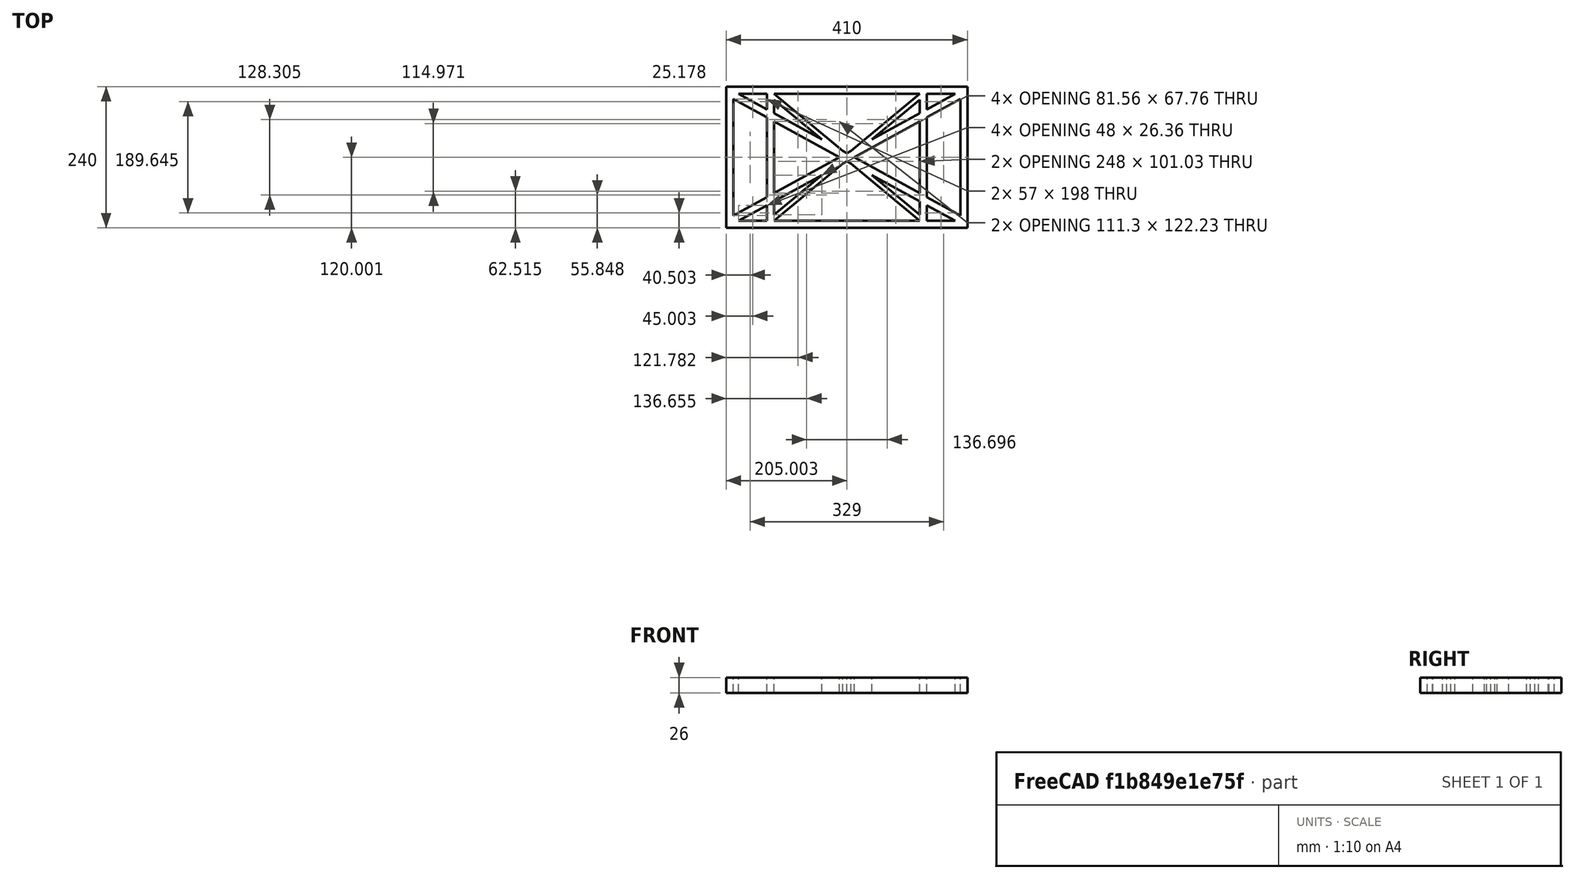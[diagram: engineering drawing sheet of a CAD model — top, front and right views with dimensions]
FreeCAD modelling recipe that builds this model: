
FCSTD DOCUMENT  (FreeCAD 0.19R0.19.2)
Label: laptopStand025
License: All rights reserved
LicenseURL: http://en.wikipedia.org/wiki/All_rights_reserved
objects: Sketcher::SketchObject×3, Part::Extrusion×1
note: 4 computed .brp shape members not serialized (recipe doc carries the construction recipe); baked Part::Feature solids carry a one-line shape summary decoded from their .brp

FEATURE [Sketcher::SketchObject] Sketch
  FullyConstrained = true
  sketch-geometry (52):
    g0: LineSegment StartX=-22.9272 StartY=136.221 StartZ=0 EndX=-22.9272 EndY=-103.779 EndZ=0
    g1: LineSegment StartX=-22.9272 StartY=136.221 StartZ=0 EndX=387.073 EndY=136.221 EndZ=0
    g2: LineSegment StartX=-22.9272 StartY=-103.779 StartZ=0 EndX=387.073 EndY=-103.779 EndZ=0
    g3: LineSegment StartX=387.073 StartY=136.221 StartZ=0 EndX=387.073 EndY=-103.779 EndZ=0
    g4: LineSegment StartX=375.073 StartY=115.221 StartZ=0 EndX=318.073 EndY=83.9235 EndZ=0
    g5: LineSegment StartX=-10.9272 StartY=-82.7794 StartZ=0 EndX=46.0728 EndY=-51.4823 EndZ=0
    g6: LineSegment StartX=-1.92719 StartY=124.221 StartZ=0 EndX=46.0728 EndY=97.8651 EndZ=0
    g7: LineSegment StartX=366.073 StartY=-91.7794 StartZ=0 EndX=318.073 EndY=-65.424 EndZ=0
    g8: LineSegment StartX=-10.9272 StartY=115.221 StartZ=0 EndX=-10.9272 EndY=-82.7794 EndZ=0
    g9: LineSegment StartX=375.073 StartY=-82.7794 StartZ=0 EndX=375.073 EndY=115.221 EndZ=0
    g10: LineSegment StartX=-1.92719 StartY=-91.7794 StartZ=0 EndX=46.0728 EndY=-91.7794 EndZ=0
    g11: LineSegment StartX=318.073 StartY=124.221 StartZ=0 EndX=366.073 EndY=124.221 EndZ=0
    g12: LineSegment StartX=306.073 StartY=-81.8102 StartZ=0 EndX=224.513 EndY=-14.0532 EndZ=0
    g13: LineSegment StartX=58.0728 StartY=114.251 StartZ=0 EndX=139.632 EndY=46.4944 EndZ=0
    g14: LineSegment StartX=306.073 StartY=124.221 StartZ=0 EndX=189.124 EndY=27.0628 EndZ=0
    g15: LineSegment StartX=58.0728 StartY=-91.7794 StartZ=0 EndX=175.022 EndY=5.37834 EndZ=0
    g16: LineSegment StartX=46.0728 StartY=124.221 StartZ=0 EndX=46.0728 EndY=97.8651 EndZ=0
    g17: LineSegment StartX=58.0728 StartY=-81.8102 StartZ=0 EndX=58.0728 EndY=-58.8351 EndZ=0
    g18: LineSegment StartX=318.073 StartY=124.221 StartZ=0 EndX=318.073 EndY=97.8651 EndZ=0
    g19: LineSegment StartX=306.073 StartY=114.251 StartZ=0 EndX=306.073 EndY=91.2763 EndZ=0
    g20: LineSegment StartX=182.073 StartY=23.1914 StartZ=0 EndX=189.124 EndY=27.0628 EndZ=0
    g21: LineSegment StartX=182.073 StartY=9.24976 StartZ=0 EndX=175.022 EndY=5.37834 EndZ=0
    g22: LineSegment StartX=224.513 StartY=46.4944 StartZ=0 EndX=306.073 EndY=114.251 EndZ=0
    g23: LineSegment StartX=175.022 StartY=27.0628 StartZ=0 EndX=58.0728 EndY=124.221 EndZ=0
    g24: LineSegment StartX=169.377 StartY=16.2206 StartZ=0 EndX=58.0728 EndY=77.3346 EndZ=0
    g25: LineSegment StartX=139.632 StartY=-14.0532 StartZ=0 EndX=58.0728 EndY=-81.8102 EndZ=0
    g26: LineSegment StartX=194.768 StartY=16.2206 StartZ=0 EndX=306.073 EndY=-44.8935 EndZ=0
    g27: LineSegment StartX=224.513 StartY=46.4944 StartZ=0 EndX=306.073 EndY=91.2763 EndZ=0
    g28: LineSegment StartX=175.022 StartY=27.0628 StartZ=0 EndX=182.073 EndY=23.1914 EndZ=0
    g29: LineSegment StartX=139.632 StartY=-14.0532 StartZ=0 EndX=58.0728 EndY=-58.8351 EndZ=0
    g30: LineSegment StartX=189.124 StartY=5.37834 StartZ=0 EndX=182.073 EndY=9.24976 EndZ=0
    g31: LineSegment StartX=189.124 StartY=5.37834 StartZ=0 EndX=306.073 EndY=-91.7794 EndZ=0
    g32: LineSegment StartX=306.073 StartY=77.3346 StartZ=0 EndX=306.073 EndY=-44.8935 EndZ=0
    g33: LineSegment StartX=318.073 StartY=83.9235 StartZ=0 EndX=318.073 EndY=-51.4823 EndZ=0
    g34: LineSegment StartX=318.073 StartY=97.8651 StartZ=0 EndX=366.073 EndY=124.221 EndZ=0
    g35: LineSegment StartX=306.073 StartY=77.3346 StartZ=0 EndX=194.768 EndY=16.2206 EndZ=0
    g36: LineSegment StartX=306.073 StartY=-58.8351 StartZ=0 EndX=224.513 EndY=-14.0532 EndZ=0
    g37: LineSegment StartX=306.073 StartY=-58.8351 StartZ=0 EndX=306.073 EndY=-81.8102 EndZ=0
    g38: LineSegment StartX=318.073 StartY=-51.4823 StartZ=0 EndX=375.073 EndY=-82.7794 EndZ=0
    g39: LineSegment StartX=318.073 StartY=-65.424 StartZ=0 EndX=318.073 EndY=-91.7794 EndZ=0
    g40: LineSegment StartX=306.073 StartY=124.221 StartZ=0 EndX=58.0728 EndY=124.221 EndZ=0
    g41: LineSegment StartX=318.073 StartY=-91.7794 StartZ=0 EndX=366.073 EndY=-91.7794 EndZ=0
    g42: LineSegment StartX=58.0728 StartY=-91.7794 StartZ=0 EndX=306.073 EndY=-91.7794 EndZ=0
    g43: LineSegment StartX=58.0728 StartY=-44.8935 StartZ=0 EndX=58.0728 EndY=77.3346 EndZ=0
    g44: LineSegment StartX=46.0728 StartY=-65.424 StartZ=0 EndX=-1.92719 EndY=-91.7794 EndZ=0
    g45: LineSegment StartX=46.0728 StartY=-65.424 StartZ=0 EndX=46.0728 EndY=-91.7794 EndZ=0
    g46: LineSegment StartX=58.0728 StartY=-44.8935 StartZ=0 EndX=169.377 EndY=16.2206 EndZ=0
    g47: LineSegment StartX=58.0728 StartY=91.2763 StartZ=0 EndX=58.0728 EndY=114.251 EndZ=0
    g48: LineSegment StartX=46.0728 StartY=83.9235 StartZ=0 EndX=46.0728 EndY=-51.4823 EndZ=0
    g49: LineSegment StartX=46.0728 StartY=124.221 StartZ=0 EndX=-1.92719 EndY=124.221 EndZ=0
    g50: LineSegment StartX=58.0728 StartY=91.2763 StartZ=0 EndX=139.632 EndY=46.4944 EndZ=0
    g51: LineSegment StartX=46.0728 StartY=83.9235 StartZ=0 EndX=-10.9272 EndY=115.221 EndZ=0
  constraints (102):
    c: Vertical(g0)
    c: Distance(g0) = 240
    c: Horizontal(g1)
    c: Distance(g1) = 410
    c: Coincident(g1,g0)
    c: Coincident(g2,g0)
    c: Horizontal(g2)
    c: Coincident(g3,g1)
    c: Vertical(g3)
    c: Coincident(g2,g3)
    c: Block(g1)
    c: Horizontal(g10)
    c: Horizontal(g11)
    c: PointOnObject(g35,g6)
    c: Coincident(g28,g20)
    c: Coincident(g30,g21)
    c: Tangent(g7,g24)
    c: PointOnObject(g24,g5)
    c: PointOnObject(g26,g4)
    c: Coincident(g20,g14)
    c: Tangent(g20,g27)
    c: Coincident(g50,g13)
    c: Coincident(g28,g23)
    c: Coincident(g22,g27)
    c: Coincident(g21,g15)
    c: Coincident(g29,g25)
    c: Tangent(g21,g29)
    c: Coincident(g36,g12)
    c: Coincident(g31,g30)
    c: Coincident(g22,g19)
    c: Tangent(g19,g32)
    c: Tangent(g18,g33)
    c: Coincident(g27,g19)
    c: Tangent(g27,g34)
    c: Coincident(g4,g33)
    c: Coincident(g35,g32)
    c: Tangent(g4,g35)
    c: Coincident(g37,g12)
    c: Tangent(g7,g36)
    c: Tangent(g32,g37)
    c: Coincident(g26,g32)
    c: Tangent(g26,g38)
    c: Coincident(g33,g38)
    c: Coincident(g39,g7)
    c: Tangent(g33,g39)
    c: Coincident(g25,g17)
    c: Tangent(g17,g43)
    c: Coincident(g29,g17)
    c: Tangent(g29,g44)
    c: Coincident(g45,g44)
    c: Tangent(g16,g45)
    c: Coincident(g5,g48)
    c: Coincident(g46,g43)
    c: Tangent(g5,g46)
    c: Tangent(g43,g47)
    c: Tangent(g16,g48)
    c: Coincident(g13,g47)
    c: PointOnObject(g40,g23)
    c: Tangent(g40,g49)
    c: Coincident(g6,g16)
    c: Coincident(g50,g47)
    c: Tangent(g6,g50)
    c: Coincident(g24,g43)
    c: Coincident(g51,g48)
    c: Tangent(g24,g51)
    c: Block(g23)
    c: Block(g14)
    c: Block(g20)
    c: Block(g40)
    c: Block(g18)
    c: Block(g34)
    c: Block(g4)
    c: Block(g38)
    c: Block(g9)
    c: Block(g36)
    c: Block(g37)
    c: Block(g7)
    c: Block(g39)
    c: Block(g22)
    c: Block(g31)
    c: Block(g42)
    c: Block(g21)
    c: Block(g15)
    c: Block(g29)
    c: Block(g25)
    c: Block(g45)
    c: Block(g44)
    c: Block(g5)
    c: Block(g8)
    c: Block(g51)
    c: Block(g6)
    c: Block(g16)
    c: Block(g13)
    c: Block(g47)
    c: Block(g35)
    c: Block(g32)
    c: Block(g24)
    c: Block(g46)
    c: Block(g49)
    c: Block(g11)
    c: Block(g41)
    c: Block(g10)
FEATURE [Part::Extrusion] Extrude
  Base = -> Sketch
  Dir = (0,0,1)
  DirMode = 2
  FaceMakerClass = Part::FaceMakerBullseye
  LengthFwd = 26
  LengthRev = 0
  Solid = true
  Symmetric = false
FEATURE [Sketcher::SketchObject] Sketch001
  FullyConstrained = false
  MapMode = 4
  Placement = pos=(0,0,0) rot=(0.57735,0.57735,0.57735;2.0944rad)
  Support = -> [Sketch]
  sketch-geometry (29):
    g0: LineSegment StartX=17.2228 StartY=-16.0875 StartZ=0 EndX=117.223 EndY=-16.0875 EndZ=0
    g1: LineSegment StartX=17.2228 StartY=-16.0875 StartZ=0 EndX=17.2228 EndY=-19.0875 EndZ=0
    g2: LineSegment StartX=117.223 StartY=-16.0875 StartZ=0 EndX=117.223 EndY=-19.0875 EndZ=0
    g3: BSplineCurve PolesCount=3 KnotsCount=2 Degree=2 IsPeriodic=0
    g4: LineSegment StartX=94.6577 StartY=-26.1351 StartZ=0 EndX=24.2583 EndY=-213.335 EndZ=0
    g5: LineSegment StartX=-9.4377 StartY=-200.664 StartZ=0 EndX=24.2583 EndY=-213.335 EndZ=0
    g6: LineSegment StartX=-9.4377 StartY=-200.664 StartZ=0 EndX=56.1962 EndY=-26.1351 EndZ=0
    g7: LineSegment StartX=17.2228 StartY=-19.0875 StartZ=0 EndX=38.8094 EndY=-19.0875 EndZ=0
    g8: BSplineCurve PolesCount=4 KnotsCount=2 Degree=3 IsPeriodic=0
    g9: LineSegment StartX=78.0148 StartY=-19.2805 StartZ=0 EndX=73.122 EndY=-32.2909 EndZ=0
    g10: ArcOfCircle CenterX=73.122 CenterY=-32.2909 CenterZ=0 NormalX=0 NormalY=0 NormalZ=1 AngleXU=0 Radius=13 StartAngle=5.92268 EndAngle=9.06428
    g11: LineSegment StartX=73.122 StartY=-32.2909 StartZ=0 EndX=77.698 EndY=-20.1229 EndZ=0
    g12: LineSegment StartX=73.122 StartY=-32.2909 StartZ=0 EndX=65.0081 EndY=-53.8121 EndZ=0
    g13: LineSegment StartX=65.0081 StartY=-53.8121 StartZ=0 EndX=62.1899 EndY=-61.306 EndZ=0
    g14: LineSegment StartX=85.2864 StartY=-36.8765 StartZ=0 EndX=78.9505 EndY=-53.7246 EndZ=0
    g15: LineSegment StartX=60.9577 StartY=-27.7052 StartZ=0 EndX=54.6191 EndY=-44.5532 EndZ=0
    g16: ArcOfCircle CenterX=66.7816 CenterY=-49.1439 CenterZ=0 NormalX=0 NormalY=0 NormalZ=1 AngleXU=0 Radius=13 StartAngle=2.78068 EndAngle=5.92131
    g17: ArcOfCircle CenterX=97.2888 CenterY=-81.8271 CenterZ=0 NormalX=0 NormalY=0 NormalZ=1 AngleXU=0 Radius=13 StartAngle=5.92268 EndAngle=9.06428
    g18: LineSegment StartX=101.865 StartY=-69.6591 StartZ=0 EndX=97.2888 EndY=-81.8271 EndZ=0
    g19: LineSegment StartX=85.1244 StartY=-77.2415 StartZ=0 EndX=78.7885 EndY=-94.0895 EndZ=0
    g20: ArcOfCircle CenterX=90.9509 CenterY=-98.6802 CenterZ=0 NormalX=0 NormalY=0 NormalZ=1 AngleXU=0 Radius=13 StartAngle=2.78068 EndAngle=5.92131
    g21: LineSegment StartX=109.453 StartY=-86.4128 StartZ=0 EndX=103.117 EndY=-103.261 EndZ=0
    g22: LineSegment StartX=62.1899 StartY=-61.306 StartZ=0 EndX=58.4376 EndY=-71.2838 EndZ=0
    g23: ArcOfCircle CenterX=53.8616 CenterY=-83.4518 CenterZ=0 NormalX=0 NormalY=0 NormalZ=1 AngleXU=0 Radius=13 StartAngle=5.92268 EndAngle=9.06428
    g24: LineSegment StartX=41.6973 StartY=-78.8662 StartZ=0 EndX=35.3613 EndY=-95.7142 EndZ=0
    g25: ArcOfCircle CenterX=47.5238 CenterY=-100.305 CenterZ=0 NormalX=0 NormalY=0 NormalZ=1 AngleXU=0 Radius=13 StartAngle=2.78068 EndAngle=5.92131
    g26: LineSegment StartX=66.026 StartY=-88.0375 StartZ=0 EndX=59.6901 EndY=-104.886 EndZ=0
    g27: LineSegment StartX=58.4376 StartY=-71.2838 StartZ=0 EndX=53.8616 EndY=-83.4518 EndZ=0
    g28: LineSegment StartX=53.8616 StartY=-83.4518 StartZ=0 EndX=37.33 EndY=-127.411 EndZ=0
  constraints (58):
    c: Horizontal(g0)
    c: Distance(g0) = 100
    c: Block(g0)
    c: Coincident(g1,g0)
    c: Vertical(g1)
    c: Distance(g1) = 3
    c: Coincident(g2,g0)
    c: Vertical(g2)
    c: Distance(g2) = 3
    c: Block(g3)
    c: Coincident(g3,g2)
    c: Coincident(g4,g3)
    c: Block(g4)
    c: Coincident(g5,g4)
    c: Coincident(g6,g5)
    c: Coincident(g7,g1)
    c: Horizontal(g7)
    c: Block(g8)
    c: Coincident(g8,g7)
    c: Coincident(g8,g6)
    c: Block(g6)
    c: Block(g10)
    c: Coincident(g11,g10)
    c: PointOnObject(g11,g10)
    c: Coincident(g11,g9)
    c: Block(g9)
    c: Coincident(g12,g9)
    c: Coincident(g13,g12)
    c: Parallel(g4,g13)
    c: Distance(g14) = 18
    c: Coincident(g14,g10)
    c: Parallel(g4,g14)
    c: Coincident(g15,g10)
    c: Block(g16)
    c: Coincident(g16,g15)
    c: Block(g15)
    c: Equal(g14,g21) = 18
    c: Coincident(g21,g17)
    c: Coincident(g19,g17)
    c: Block(g20)
    c: Coincident(g20,g19)
    c: Block(g19)
    c: PointOnObject(g13,g16)
    c: Coincident(g22,g13)
    c: Distance(g22) = 10.66
    c: Parallel(g4,g22)
    c: Block(g17)
    c: PointOnObject(g18,g17)
    c: Coincident(g26,g23)
    c: Coincident(g24,g23)
    c: Block(g25)
    c: Coincident(g25,g24)
    c: Block(g24)
    c: Block(g23)
    c: PointOnObject(g27,g23)
    c: Coincident(g27,g22)
    c: Coincident(g28,g23)
    c: Parallel(g4,g28)
FEATURE [Sketcher::SketchObject] Sketch002
  FullyConstrained = true
  Placement = pos=(0,0,0) rot=(-1,0,0;4.71239rad)
